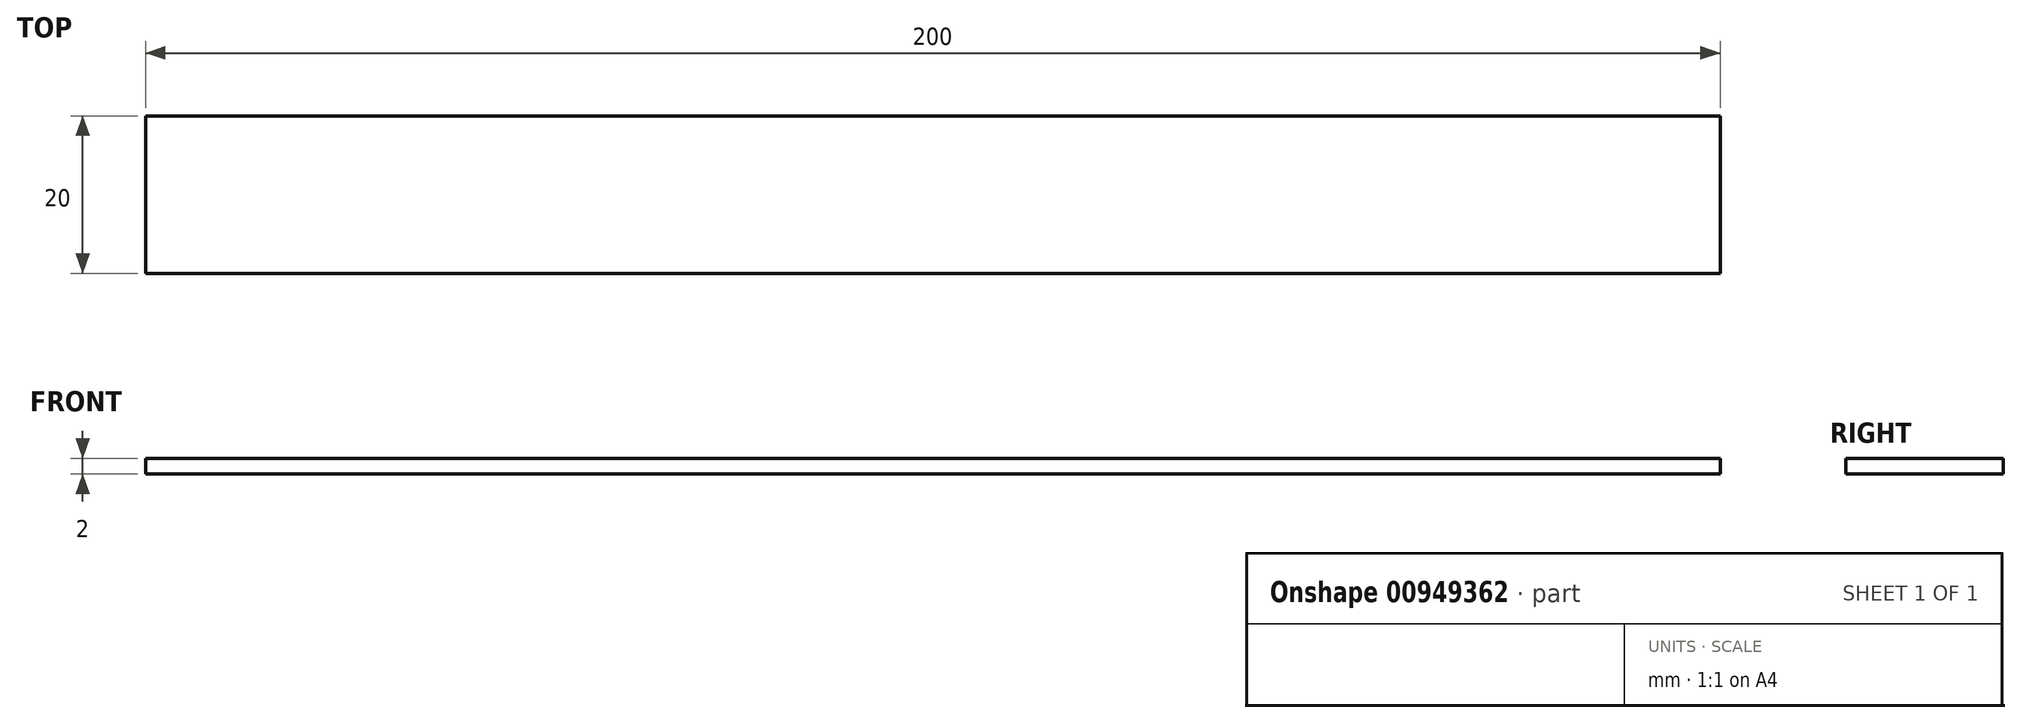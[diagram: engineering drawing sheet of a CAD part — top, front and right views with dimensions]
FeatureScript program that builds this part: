
annotation { "Feature Type Name" : "Feature", "Feature Type Description" : "" }
export const myFeature = defineFeature(function(context is Context, id is Id, definition is map)
    precondition{}
    {
        {
            var Q0;
            Q0=qCreatedBy(makeId("Top.planeOp"),FACE);
            var sketch = newSketch(context, id + "F0", { "sketchPlane" : qUnion([Q0])});
            skLineSegment(sketch, "E0.bottom", {"start": v(-100, -10) * mm, "end": v(100, -10) * mm});
            skLineSegment(sketch, "E0.top", {"start": v(-100, 10) * mm, "end": v(100, 10) * mm});
            skLineSegment(sketch, "E0.left", {"start": v(-100, -10) * mm, "end": v(-100, 10) * mm});
            skLineSegment(sketch, "E0.right", {"start": v(100, -10) * mm, "end": v(100, 10) * mm});
            skPoint(sketch, "E0.middle", {"position": v(0, 0) * mm});
            skSolve(sketch);
        }
        {
            var Q0;
            Q0=makeQuery(id+"F0.imprint","IMPRINT",FACE,{"disambiguationData":[TD([[makeQuery(id+"F0.imprint","IMPRINT",EDGE,{"derivedFrom":sQuery(id+"F0.wireOp",EDGE,"E0.bottom")}),1.0]])]});
            extrude(context, id + "F1", {"entities" : qUnion([Q0]), "depth" : 2 * mm, "offsetDistance" : 25 * mm});
        }
    });
